# Revit family: Overhead_Door-CHI-MaxDock_Manual
name_source: partatom
category: Specialty Equipment
units: mm (PartAtom-declared; Revit-internal decimal feet)

## family parameters
Always vertical = Yes
Cut with Voids When Loaded = No
Enable Cutting in Views = No
Host = Wall
Maintain Annotation Orientation = No
OmniClass Number = 23.30.10.21
OmniClass Title = Special Function Doors
Part Type = Normal
Room Calculation Point = No
Round Connector Dimension = Use Diameter
Shared = No

## types (1)
- MaxDock - 100 - Gray - 1/4" Reinforced Rubber Curtain
    Assembly Code = B2030410
    Closing Speed = Manual
    Curtain Material = Rubber - C.H.I Overhead Doors - Reinforced Black Rubber
    Default Elevation = 0' - 0"
    Description = Hight Performance Rubber Door
    Door Rail Depth = 0' - 5"
    Door Rail Width = 0' - 4"
    Keynote = 08 30 00
    Manufacturer = C.H.I. Overhead Doors
    Manufacturer Fax Number = 800-677-2650
    Model = 100
    Opening Speed = Manual
    Panel Thickness = 0' - 0 1/4"
    Product Documentation Link = https://www.chiohd.com
    Product Page URL = https://www.chiohd.com
    Shutter Box Depth = 1' - 3"
    Shutter Box Height = 1' - 1"
    Steel Gauge = 1/4"
    URL = https://www.chiohd.com
    Version = 2021-v1.a
    Warranty URL = https://www.chiohd.com

## geometry (parser evidence)
native form markers: Extrusion x1, Sweep x5
no freeform markers — native parametric forms only
